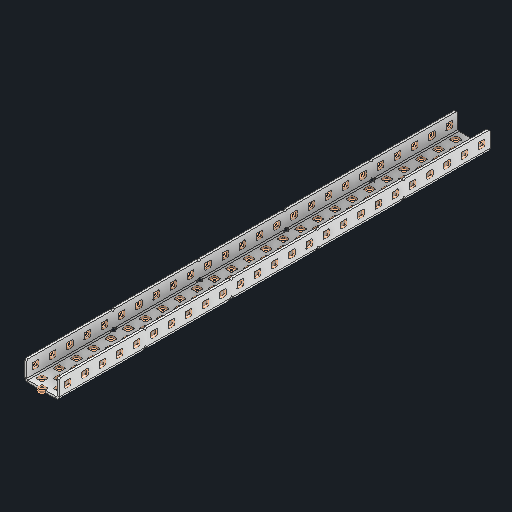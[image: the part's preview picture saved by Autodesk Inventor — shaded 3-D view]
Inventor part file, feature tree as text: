
AUTODESK INVENTOR PART (.ipt)
format: ipt  version: 2024 (Build 280153000, 153)  size: 2,035,712 bytes
history: native  units: in
note: dims shown in document units (in); Inventor stores cm internally (conversion verified against a paired STEP export)
features: other x256, sketch x5, sheet_metal_op x1
ambient origin geometry x8: Origin, YZ Plane, XZ Plane, XY Plane, X Axis, Y Axis, Z Axis, Center Point
bodies: Solid1 (feature_tree)
feature tree (262):
  other  "Alu C 1x2x1x25.ipt"
  other  "Solid1::Alu C 1x2x1x25.ipt"
  other  "TaggingFeature1"
  sketch  "Sketch1"  dims[d0=0.3937in]
  sketch  "Sketch2"  dims[d1=0.0625in]
  sketch  "Sketch3"
  other  "Flange Pattern Sketch"
  sketch  "Sketch9"
  sheet_metal_op  "Body Pattern Sketch"
  other  "Arc Length"
  sketch  "Sketch14"
  other  "Flange Pattern Plane"
  other  "Srf1"
  other  "Srf2"
  other  "Srf3"
  other  "Srf4"
  other  "Srf5"
  other  "Srf6"
  other  "Srf7"
  other  "Srf8"
  other  "Srf9"
  other  "Srf10"
  other  "Srf11"
  other  "Srf12"
  other  "Srf13"
  other  "Srf14"
  other  "Srf15"
  other  "Srf16"
  other  "Srf17"
  other  "Srf18"
  other  "Srf19"
  other  "Srf20"
  other  "Srf21"
  other  "Srf22"
  other  "Srf23"
  other  "Srf24"
  other  "Srf25"
  other  "Srf26"
  other  "Srf27"
  other  "Srf28"
  other  "Srf29"
  other  "Srf30"
  other  "Srf31"
  other  "Srf32"
  other  "Srf33"
  other  "Srf34"
  other  "Srf35"
  other  "Srf36"
  other  "Srf37"
  other  "Srf38"
  other  "Srf39"
  other  "Srf40"
  other  "Srf41"
  other  "Srf42"
  other  "Srf43"
  other  "Srf44"
  other  "Srf45"
  other  "Srf46"
  other  "Srf47"
  other  "Srf48"
  other  "Srf49"
  other  "Srf50"
  other  "Srf51"
  other  "Srf52"
  other  "Srf53"
  other  "Srf54"
  other  "Srf55"
  other  "Srf56"
  other  "Srf57"
  other  "Srf58"
  other  "Srf59"
  other  "Srf60"
  other  "Srf61"
  other  "Srf62"
  other  "Srf63"
  other  "Srf64"
  other  "Srf65"
  other  "Srf66"
  other  "Srf67"
  other  "Srf68"
  other  "Srf69"
  other  "Srf70"
  other  "Srf71"
  other  "Srf72"
  other  "Srf73"
  other  "Srf74"
  other  "Srf75"
  other  "Srf76"
  other  "Srf77"
  other  "Srf78"
  other  "Srf79"
  other  "Srf80"
  other  "Srf81"
  other  "Srf82"
  other  "Srf83"
  other  "Srf84"
  other  "Srf85"
  other  "Srf86"
  other  "Srf87"
  other  "Srf88"
  other  "Srf89"
  other  "Srf90"
  other  "Srf91"
  other  "Srf92"
  other  "Srf93"
  other  "Srf94"
  other  "Srf95"
  other  "Srf96"
  other  "Srf97"
  other  "Srf98"
  other  "Srf99"
  other  "Srf100"
  other  "Srf101"
  other  "Srf102"
  other  "Srf103"
  other  "Srf104"
  other  "Srf105"
  other  "Srf106"
  other  "Srf107"
  other  "Srf108"
  other  "Srf109"
  other  "Srf110"
  other  "Srf111"
  other  "Srf112"
  other  "Srf113"
  other  "Srf114"
  other  "Srf115"
  other  "Srf116"
  other  "Srf117"
  other  "Srf118"
  other  "Srf119"
  other  "Srf120"
  other  "Srf121"
  other  "Srf122"
  other  "Srf123"
  other  "Srf124"
  other  "Srf125"
  other  "Srf1::Derived"
  other  "Srf2::Derived"
  other  "Srf823::Derived"
  other  "Srf824::Derived"
  other  "Srf825::Derived"
  other  "Srf826::Derived"
  other  "Srf827::Derived"
  other  "Srf828::Derived"
  other  "Srf829::Derived"
  other  "Srf922::Derived"
  other  "Srf923::Derived"
  other  "Srf924::Derived"
  other  "Srf925::Derived"
  other  "Srf926::Derived"
  other  "Srf1143::Derived"
  other  "Srf1144::Derived"
  other  "Srf1145::Derived"
  other  "Srf1146::Derived"
  other  "Srf1147::Derived"
  other  "Srf1148::Derived"
  other  "Srf1149::Derived"
  other  "Srf1150::Derived"
  other  "Srf1151::Derived"
  other  "Srf1152::Derived"
  other  "Srf1153::Derived"
  other  "Srf1154::Derived"
  other  "Srf1155::Derived"
  other  "Srf1156::Derived"
  other  "Srf1157::Derived"
  other  "Srf1158::Derived"
  other  "Srf1159::Derived"
  other  "Srf1160::Derived"
  other  "Srf1161::Derived"
  other  "Srf1162::Derived"
  other  "Srf1163::Derived"
  other  "Srf1164::Derived"
  other  "Srf1165::Derived"
  other  "Srf1166::Derived"
  other  "Srf1167::Derived"
  other  "Srf1168::Derived"
  other  "Srf1169::Derived"
  other  "Srf1170::Derived"
  other  "Srf1171::Derived"
  other  "Srf1172::Derived"
  other  "Srf1173::Derived"
  other  "Srf1174::Derived"
  other  "Srf1175::Derived"
  other  "Srf1176::Derived"
  other  "Srf1177::Derived"
  other  "Srf1178::Derived"
  other  "Srf91::Derived"
  other  "Srf92::Derived"
  other  "Srf856::Derived"
  other  "Srf857::Derived"
  other  "Srf858::Derived"
  other  "Srf859::Derived"
  other  "Srf860::Derived"
  other  "Srf861::Derived"
  other  "Srf862::Derived"
  other  "Srf959::Derived"
  other  "Srf960::Derived"
  other  "Srf961::Derived"
  other  "Srf962::Derived"
  other  "Srf963::Derived"
  other  "Srf1199::Derived"
  other  "Srf1200::Derived"
  other  "Srf1201::Derived"
  other  "Srf1202::Derived"
  other  "Srf1203::Derived"
  other  "Srf1204::Derived"
  other  "Srf1205::Derived"
  other  "Srf1206::Derived"
  other  "Srf1207::Derived"
  other  "Srf1208::Derived"
  other  "Srf1209::Derived"
  other  "Srf1210::Derived"
  other  "Srf1211::Derived"
  other  "Srf1212::Derived"
  other  "Srf1213::Derived"
  other  "Srf1214::Derived"
  other  "Srf1215::Derived"
  other  "Srf1216::Derived"
  other  "Srf1217::Derived"
  other  "Srf1218::Derived"
  other  "Srf1219::Derived"
  other  "Srf1220::Derived"
  other  "Srf1221::Derived"
  other  "Srf1222::Derived"
  other  "Srf1223::Derived"
  other  "Srf1224::Derived"
  other  "Srf1225::Derived"
  other  "Srf1226::Derived"
  other  "Srf1227::Derived"
  other  "Srf1228::Derived"
  other  "Srf1229::Derived"
  other  "Srf1230::Derived"
  other  "Srf1231::Derived"
  other  "Srf1232::Derived"
  other  "Srf1233::Derived"
  other  "Srf1234::Derived"
  other  "Srf786::Derived"
  other  "Srf889::Derived"
  other  "Srf890::Derived"
  other  "Srf891::Derived"
  other  "Srf892::Derived"
  other  "Srf893::Derived"
  other  "Srf894::Derived"
  other  "Srf895::Derived"
  other  "Srf896::Derived"
  other  "Srf996::Derived"
  other  "Srf997::Derived"
  other  "Srf998::Derived"
  other  "Srf999::Derived"
  other  "Srf1000::Derived"
  other  "Srf1255::Derived"
  other  "Srf1256::Derived"
  other  "Srf1257::Derived"
  other  "Srf1258::Derived"
  other  "Srf1259::Derived"
  other  "Srf1260::Derived"
  other  "Srf1261::Derived"
  other  "Srf1262::Derived"
  other  "Srf1263::Derived"
  other  "Srf1264::Derived"
  other  "Srf1265::Derived"
